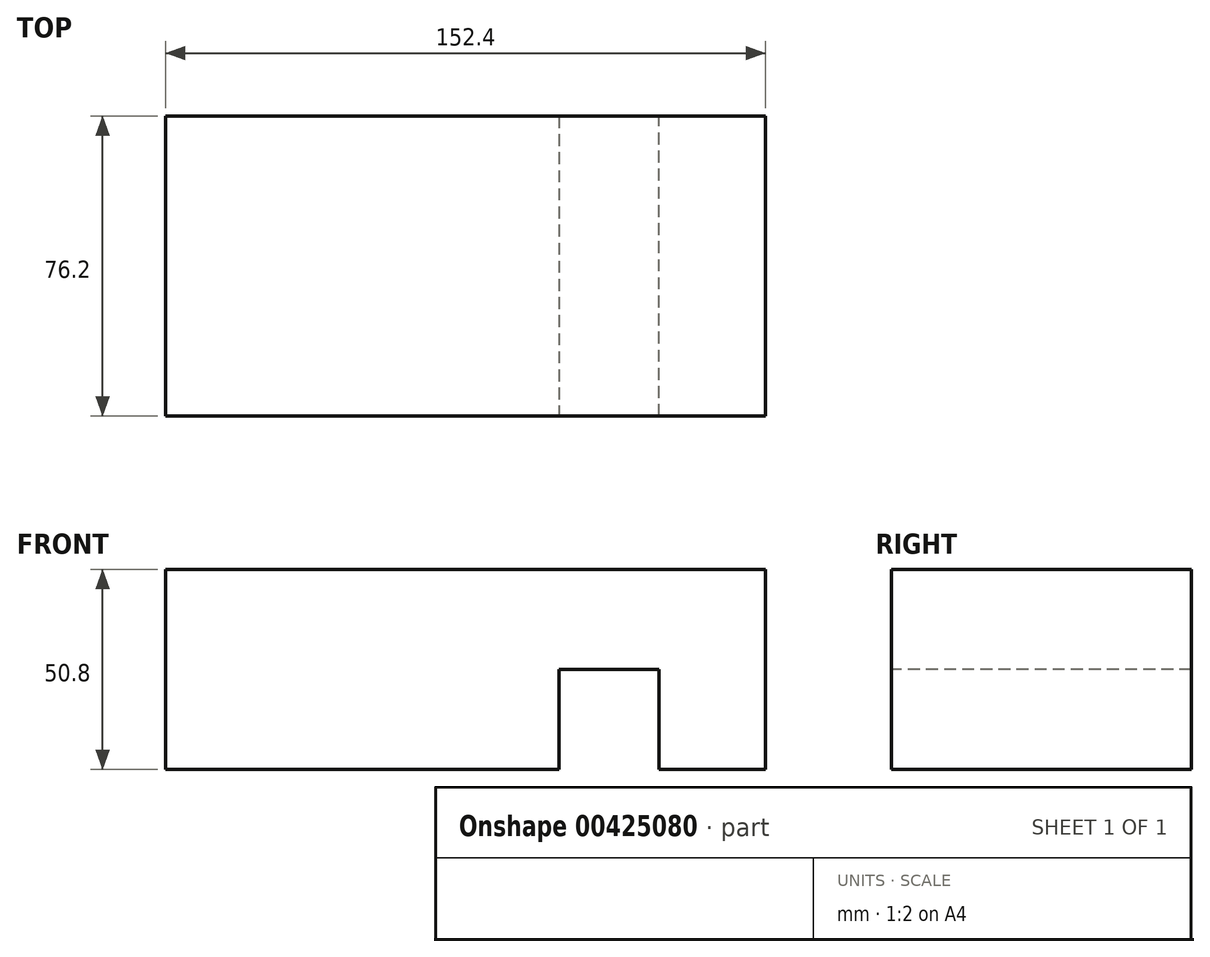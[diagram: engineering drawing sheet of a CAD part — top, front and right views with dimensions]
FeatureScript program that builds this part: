
annotation { "Feature Type Name" : "Feature", "Feature Type Description" : "" }
export const myFeature = defineFeature(function(context is Context, id is Id, definition is map)
    precondition{}
    {
        {
            var Q0;
            Q0=qCreatedBy(makeId("Front.planeOp"),FACE);
            var sketch = newSketch(context, id + "F0", { "sketchPlane" : qUnion([Q0])});
            skLineSegment(sketch, "E0", {"start": v(0, 0) * mm, "end": v(152.4, 0) * mm});
            skLineSegment(sketch, "E1", {"start": v(152.4, 0) * mm, "end": v(152.4, 50.8) * mm});
            skLineSegment(sketch, "E2", {"start": v(152.4, 50.8) * mm, "end": v(0, 50.8) * mm});
            skLineSegment(sketch, "E3", {"start": v(0, 50.8) * mm, "end": v(0, 0) * mm});
            skSolve(sketch);
        }
        {
            var Q0;
            Q0=makeQuery(id+"F0.imprint","IMPRINT",FACE,{"disambiguationData":[TD([[makeQuery(id+"F0.imprint","IMPRINT",EDGE,{"derivedFrom":sQuery(id+"F0.wireOp",EDGE,"E0")}),1.0]])]});
            extrude(context, id + "F1", {"entities" : qUnion([Q0]), "depth" : 76.2 * mm});
        }
        {
            var Q0;
            Q0=qCreatedBy(makeId("Top.planeOp"),FACE);
            var sketch = newSketch(context, id + "F2", { "sketchPlane" : qUnion([Q0])});
            skLineSegment(sketch, "E4", {"start": v(99.89, 0) * mm, "end": v(99.89, -76.23) * mm});
            skLineSegment(sketch, "E5", {"start": v(99.89, -76.23) * mm, "end": v(125.29, -76.23) * mm});
            skLineSegment(sketch, "E6", {"start": v(125.29, -76.23) * mm, "end": v(125.29, 0) * mm});
            skLineSegment(sketch, "E7", {"start": v(125.29, 0) * mm, "end": v(99.89, 0) * mm});
            skSolve(sketch);
        }
        {
            var Q0;
            Q0 = qSketchRegion(id + "F2", true);
            extrude(context, id + "F3", {"entities" : qUnion([Q0]), "operationType" : NewBodyOperationType.REMOVE, "depth" : 25.4 * mm});
        }
    });
